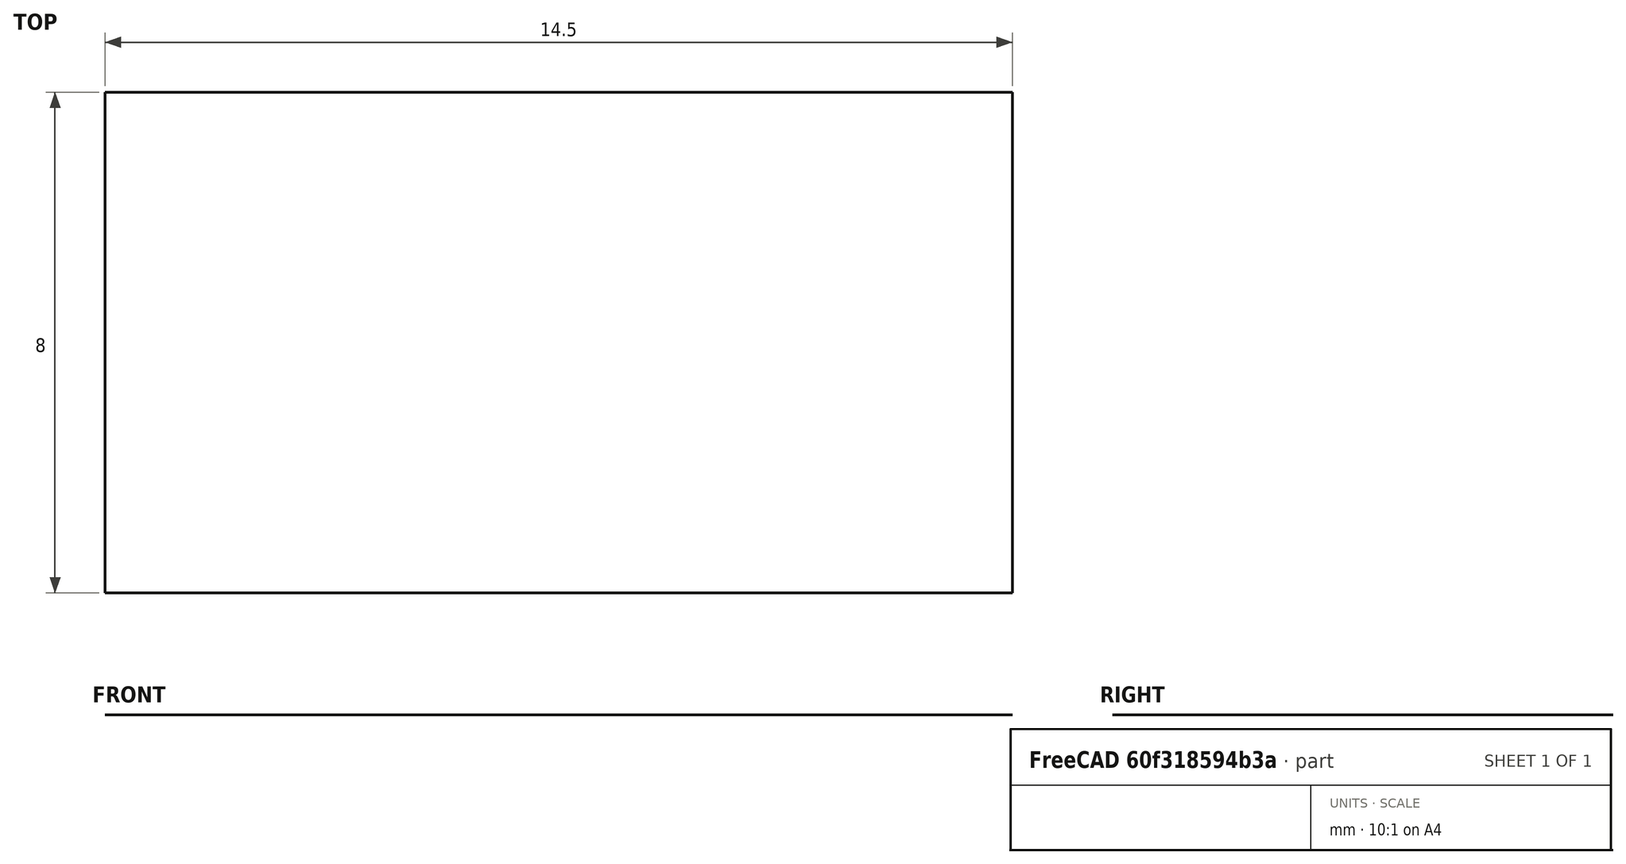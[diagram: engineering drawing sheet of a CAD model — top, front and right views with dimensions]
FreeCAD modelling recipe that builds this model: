
FCSTD DOCUMENT  (FreeCAD 0.20R29177 (Git))
Label: sensor_plane
License: All rights reserved
LicenseURL: http://en.wikipedia.org/wiki/All_rights_reserved
objects: Sketcher::SketchObject×1, Part::Face×1
note: 2 computed .brp shape members not serialized (recipe doc carries the construction recipe); baked Part::Feature solids carry a one-line shape summary decoded from their .brp

FEATURE [Sketcher::SketchObject] Sketch
  FullyConstrained = true
  sketch-geometry (4):
    g0: LineSegment StartX=0 StartY=0 StartZ=0 EndX=14.5 EndY=0 EndZ=0
    g1: LineSegment StartX=14.5 StartY=0 StartZ=0 EndX=14.5 EndY=-8 EndZ=0
    g2: LineSegment StartX=14.5 StartY=-8 StartZ=0 EndX=0 EndY=-8 EndZ=0
    g3: LineSegment StartX=0 StartY=-8 StartZ=0 EndX=0 EndY=0 EndZ=0
  constraints (11):
    c: Coincident(g0,g1)
    c: Coincident(g1,g2)
    c: Coincident(g2,g3)
    c: Coincident(g3,g0)
    c: Horizontal(g0)
    c: Horizontal(g2)
    c: Vertical(g1)
    c: Vertical(g3)
    c: Coincident(g0,g-1)
    c: DistanceX(g0,g0) = 14.5
    c: DistanceY(g1,g1) = 8
FEATURE [Part::Face] Face
  FaceMakerClass = Part::FaceMakerBullseye
  Sources = -> [Sketch]
